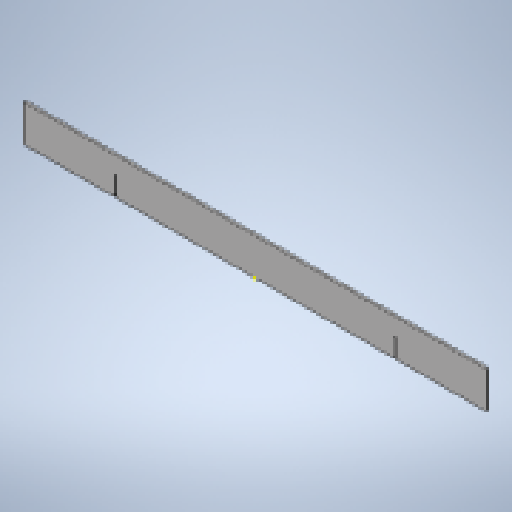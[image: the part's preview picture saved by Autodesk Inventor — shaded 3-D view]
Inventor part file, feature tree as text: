
AUTODESK INVENTOR PART (.ipt)
format: ipt  version: 2025 (Build 290162010, 162A)  size: 225,280 bytes
history: native  units: mm
features: sketch x4, extrude x2, other x2, sheet_metal_op x1, projected_geometry x1
ambient origin geometry x8: Origin, YZ Plane, XZ Plane, XY Plane, X Axis, Y Axis, Z Axis, Center Point
bodies: Body1 (feature_tree)
feature tree (10):
  sheet_metal_op  "Face1"
  extrude  "Extrusion1"  Depth=50.0mm
  extrude  "Extrusion2"  Depth=3.0mm
  other  "Mark1"
  sketch  "Sketch2"  dims[d18=750.0mm d19=50.0mm]
  other  "Plate2"
  sketch  "Sketch3"  dims[d20=45.0mm d21=3.0mm]
  sketch  "Sketch4"  dims[d23=3.0mm]
  projected_geometry  "Projected Loop1"
  sketch  "Sketch5"  dims[d24=26.0mm d25=0.0mm d26=0.0mm d30=190.0mm d31=190.0mm d32=3.0mm d33=26.0mm d35=60.0mm d36=60.0mm d37=0.0mm d38=0.0mm]
